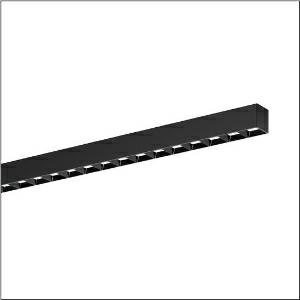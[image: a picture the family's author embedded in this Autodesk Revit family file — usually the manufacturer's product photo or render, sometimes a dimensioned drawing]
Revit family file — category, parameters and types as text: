
# Revit family: silica_21_51mx24tctab
name_source: partatom
category: Lighting Fixtures
units: mm (PartAtom-declared; Revit-internal decimal feet)

## family parameters
Cut with Voids When Loaded = No
Host = Face
Light Source = No
Part Type = Normal
Room Calculation Point = No
Round Connector Dimension = Use Diameter
Shared = No

## types (1)
- --- (1 x LED, 8200 lm, 81.1 W, 6500K)
    Apparent Load = 81 VA
    CIE Flux Codes = 74 94 99 100 100
    Color Rendering = 80
    Color Temperature = 6500K
    Default Elevation = 1800 mm
    Description = Silica 21, office luminaire, primary light control with darklight reflector, of PMMA, black, light emission: direct distribution, primary light characteristic: asymmetric, installation type: surface-mounted, LED, rated luminous flux: 8.200lm, luminous efficacy: 96lm/W, light colour: 8tw, colour temperature: 2700..6500K, control gear: DALI DT8, with terminal, 3+2-pole, max. 2.5mm², mains connection: 220..240V, AC, 50/60Hz, rated input power: 85.2W, luminaire housing, of aluminium, matt jet black (RAL 9005), length: 3.004mm, width: 53mm, height: 53mm, protection rating (complete): IP20, insulation class (complete): insulation class I (protective earthing), certification: CE, permissible operating ambient temperature: 0..+35°C, standard: EN 50419, packaging unit: 1 piece
    Height = 53 mm
    Lamp = 1 x LED
    Lamp Light Flux = 8200 lm
    Lamp Power = 81.1 W
    Lamp count = 1
    Length = 3004 mm
    Luminous efficacy = 101 lm/W
    Manufacturer = Siteco
    ModVariant = No
    Model = 51MX24TCTAB
    Mounting Place = Ceiling
    Mounting Type = Surface mounted
    Number of Poles = 1
    OnlyDefault = Yes
    Power Factor = 1
    Product Name = Silica 21
    Product group = office luminaire | ceiling mounted
    ProductGroupID = 301
    Protection Class = Protection class I
    Protection Degree = IP 20
    RLX_Detail_Level = 1
    RLX_Emergency_Light_Flux = 0 lm
    RLX_Emergency_Type = 0
    RLX_Emergency_Type_DB = No
    RlxData = <blob elided: 60525 chars, md5=ab97a77d>
    Socket = socket
    Standby Power = 0 W
    System Light Flux = 8200 lm
    System Power = 81 W
    Type Comments = individual setting
    Type Image = l_1335908.jpg
    URL = http://relux.com
    VarID = @adj_139481
    Voltage = 0 V
    Weight = 0.00 kg
    Width = 53 mm

## geometry (parser evidence)
native form markers: Blend x4, Sweep x11
no freeform markers — native parametric forms only
